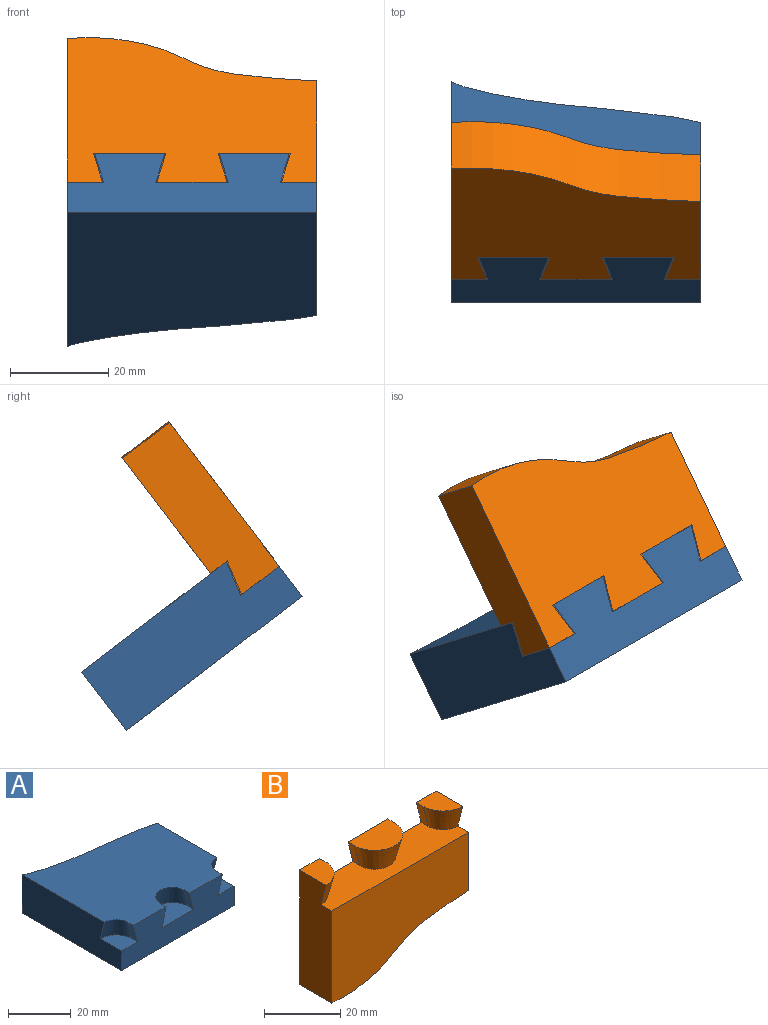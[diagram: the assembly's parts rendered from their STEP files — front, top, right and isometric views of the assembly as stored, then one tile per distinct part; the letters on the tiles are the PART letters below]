
ASSEMBLY  parts=2 mates=1
PART A: 16 faces, bbox 50.8x45.1x15 mm
  f0: plane 45.1x15mm, normal (-1,0,0), area 613.1mm2, adj f1,f2,f4,f5,f7,f8
  f1: plane 50.8x15mm, normal (0,-1,0), area 580.3mm2, adj f0,f2,f3,f4,f6,f7,f10,f11
  f2: plane 50.8x45.1mm, normal (0,0,1), area 1849.6mm2, adj f0,f1,f3,f5,f6,f8,f9,f10
  f3: plane 34.58x15mm, normal (1,0,0), area 455.3mm2, adj f1,f2,f4,f5,f13,f15
  f4: plane 50.8x45.1mm, normal (0,0,-1), area 1991.3mm2, adj f0,f1,f3,f5
  f5: extruded ~50.8x15mm, area 781.2mm2, adj f0,f2,f3,f4
  f6: plane 7.29x2.48mm, normal (-0.97,0,-0.24), area 18.6mm2, adj f1,f2,f7,f8
  f7: plane 9.62x7.14mm, normal (0,0,1), area 57.8mm2, adj f0,f1,f6,f8
  f8: cone r=5.32mm half-angle=14deg, axis (0,0,-1), area 73.5mm2, adj f0,f2,f6,f7
  f9: cone r=5.32mm half-angle=14deg, axis (0,0,-1), area 147.1mm2, adj f2,f10,f11,f12
  f10: plane 7.29x2.48mm, normal (0.97,0,-0.24), area 18.6mm2, adj f1,f2,f9,f12
  f11: plane 7.29x2.48mm, normal (-0.97,0,-0.24), area 18.6mm2, adj f1,f2,f9,f12
  f12: plane 14.29x9.62mm, normal (0,0,1), area 115.5mm2, adj f1,f9,f10,f11
  f13: plane 9.62x7.14mm, normal (0,0,1), area 57.8mm2, adj f1,f3,f14,f15
  f14: plane 7.29x2.48mm, normal (0.97,0,-0.24), area 18.6mm2, adj f1,f2,f13,f15
  f15: cone r=5.32mm half-angle=14deg, axis (0,0,-1), area 73.5mm2, adj f2,f3,f13,f14
PART B: 16 faces, bbox 50.8x12x37.4 mm
  f0: plane 9.85x7.38mm, normal (0,0,1), area 61mm2, adj f4,f6,f11,f12
  f1: plane 9.85x7.38mm, normal (0,0,1), area 61mm2, adj f4,f5,f8,f10
  f2: plane 14.76x9.85mm, normal (0,0,1), area 122mm2, adj f4,f13,f14,f15
  f3: plane 50.8x30.12mm, normal (0,-1,0), area 1227.5mm2, adj f5,f6,f7,f9
  f4: plane 50.8x37.41mm, normal (0,1,0), area 1416mm2, adj f0,f1,f2,f5,f6,f7,f9,f10
  f5: plane 36.86x12mm, normal (-1,0,0), area 420.1mm2, adj f1,f3,f4,f7,f8,f9
  f6: plane 25.97x12mm, normal (1,0,0), area 289.3mm2, adj f0,f3,f4,f7,f9,f11
  f7: extruded ~50.8x12mm, area 632.7mm2, adj f3,f4,f5,f6
  f8: cone r=7.38mm half-angle=14deg, axis (0,0,1), area 76.3mm2, adj f1,f5,f9,f10
  f9: plane 50.8x12mm, normal (0,0,1), area 457.6mm2, adj f3,f4,f5,f6,f8,f10,f11,f12
  f10: plane 7.29x2.48mm, normal (0.97,0,-0.24), area 18.6mm2, adj f1,f4,f8,f9
  f11: cone r=7.38mm half-angle=14deg, axis (0,0,1), area 76.3mm2, adj f0,f6,f9,f12
  f12: plane 7.29x2.48mm, normal (-0.97,0,-0.24), area 18.6mm2, adj f0,f4,f9,f11
  f13: plane 7.29x2.48mm, normal (0.97,0,-0.24), area 18.6mm2, adj f2,f4,f9,f15
  f14: plane 7.29x2.48mm, normal (-0.97,0,-0.24), area 18.6mm2, adj f2,f4,f9,f15
  f15: cone r=7.38mm half-angle=14deg, axis (0,0,1), area 152.6mm2, adj f2,f9,f13,f14
PLACE A rot(axis=(-1,0,0),37.4deg) t=(-21.78,-16.32,-95.02)mm
PLACE B rot(axis=(1,0,0),142.6deg) t=(-34.48,-2.52,-76.98)mm
MATE fastened B.f4 <-> A.f1  axis (0,-0.79,0.61) through (-34.48,-11.64,-88.89)mm
